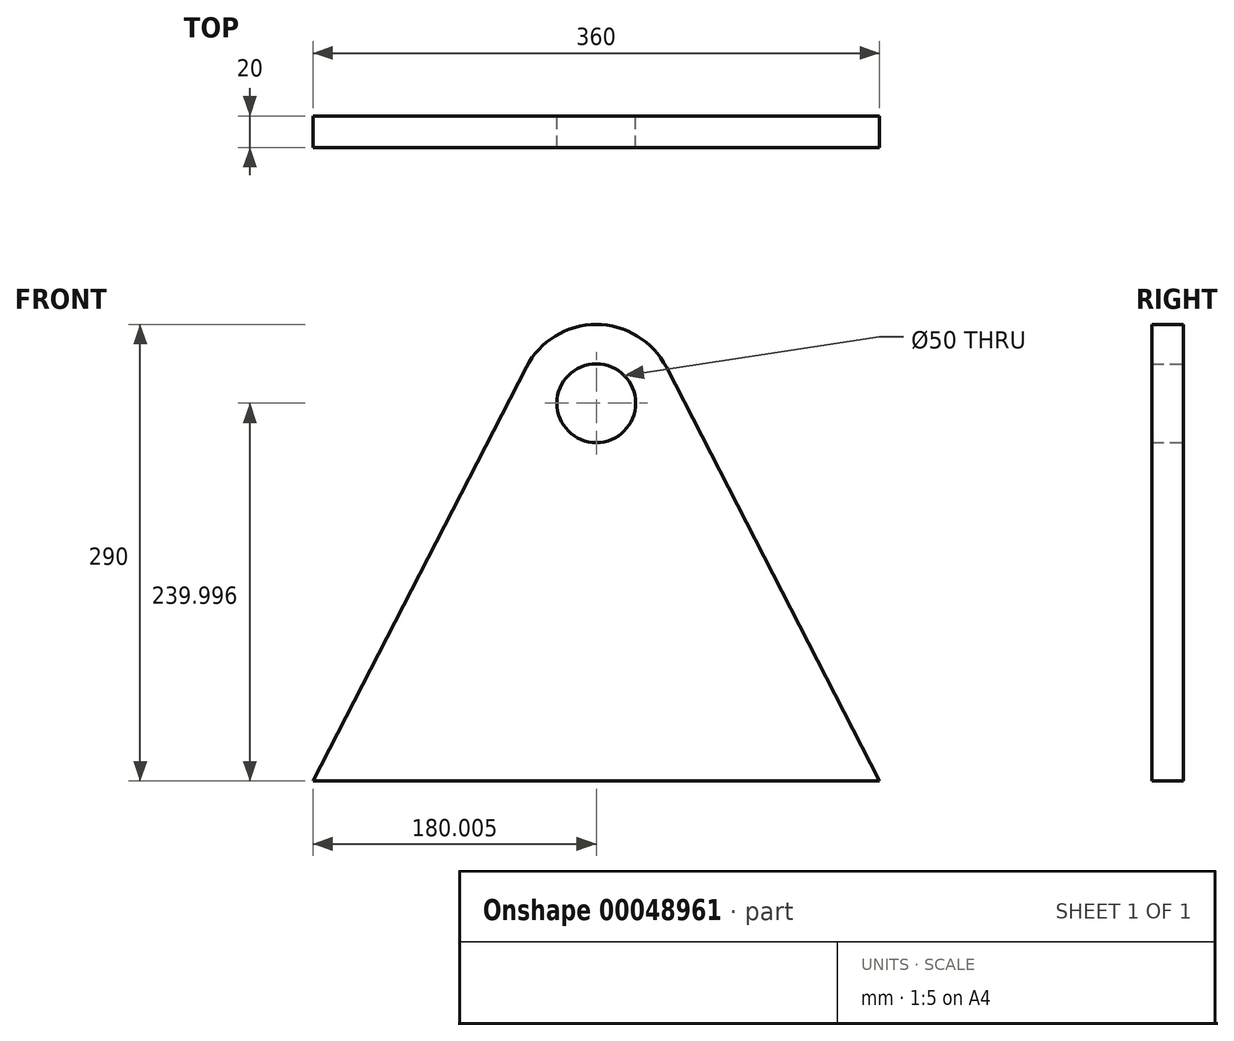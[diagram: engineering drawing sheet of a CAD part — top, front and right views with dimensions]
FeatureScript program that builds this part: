
annotation { "Feature Type Name" : "Feature", "Feature Type Description" : "" }
export const myFeature = defineFeature(function(context is Context, id is Id, definition is map)
    precondition{}
    {
        {
            var Q0;
            Q0=qCreatedBy(makeId("Front.planeOp"),FACE);
            var sketch = newSketch(context, id + "F0", { "sketchPlane" : qUnion([Q0])});
            skLineSegment(sketch, "E0", {"start": v(-126.07, 2.14) * mm, "end": v(-76.07, 2.14) * mm, "construction": true});
            skLineSegment(sketch, "E1", {"start": v(53.93, -237.86) * mm, "end": v(-126.07, -237.86) * mm});
            skArc(sketch, "E2", {"start": v(-81.62, 25.05) * mm, "mid": v(-100.04, 44.83) * mm, "end": v(-126.07, 52.14) * mm});
            skLineSegment(sketch, "E3", {"start": v(53.93, -237.86) * mm, "end": v(-81.62, 25.05) * mm});
            skLineSegment(sketch, "E4", {"start": v(-126.07, -237.86) * mm, "end": v(-126.07, 52.14) * mm, "construction": true});
            skLineSegment(sketch, "E5.MirrorCS", {"start": v(-306.07, -237.86) * mm, "end": v(-170.5, 25.05) * mm});
            skLineSegment(sketch, "E6.MirrorCS", {"start": v(-306.07, -237.86) * mm, "end": v(-126.07, -237.86) * mm});
            skArc(sketch, "E7.MirrorCS", {"start": v(-170.5, 25.05) * mm, "mid": v(-152.09, 44.83) * mm, "end": v(-126.07, 52.14) * mm});
            skCircle(sketch, "E8", {"center": v(-126.07, 2.14) * mm, "radius": 25 * mm});
            skSolve(sketch);
        }
        {
            var Q0;
            Q0=makeQuery(id+"F0.imprint","IMPRINT",FACE,{"disambiguationData":[TD([[makeQuery(id+"F0.imprint","IMPRINT",EDGE,{"derivedFrom":sQuery(id+"F0.wireOp",EDGE,"E1")}),-1.0]])]});
            extrude(context, id + "F1", {"entities" : qUnion([Q0]), "depth" : 20 * mm});
        }
    });
